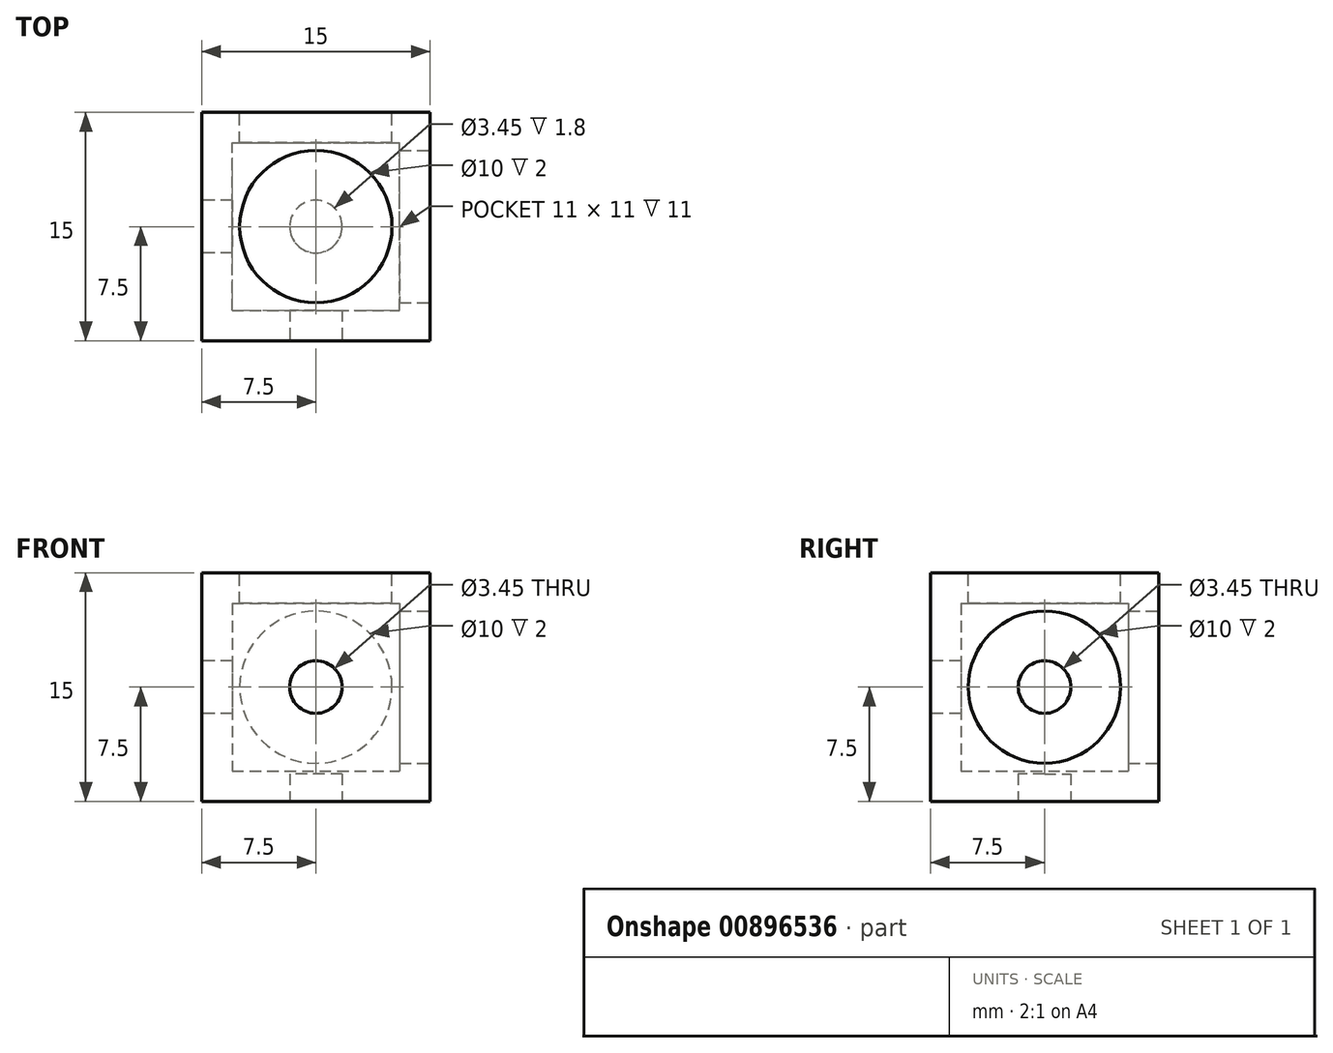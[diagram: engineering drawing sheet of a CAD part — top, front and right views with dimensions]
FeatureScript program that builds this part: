
annotation { "Feature Type Name" : "Feature", "Feature Type Description" : "" }
export const myFeature = defineFeature(function(context is Context, id is Id, definition is map)
    precondition{}
    {
        {
            var Q0;
            Q0=qCreatedBy(makeId("Top.planeOp"),FACE);
            var sketch = newSketch(context, id + "F0", { "sketchPlane" : qUnion([Q0])});
            skLineSegment(sketch, "E0.bottom", {"start": v(0, 0) * mm, "end": v(15, 0) * mm});
            skLineSegment(sketch, "E0.top", {"start": v(0, 15) * mm, "end": v(15, 15) * mm});
            skLineSegment(sketch, "E0.left", {"start": v(0, 0) * mm, "end": v(0, 15) * mm});
            skLineSegment(sketch, "E0.right", {"start": v(15, 0) * mm, "end": v(15, 15) * mm});
            skSolve(sketch);
        }
        {
            var Q0;
            Q0 = qSketchRegion(id + "F0", true);
            extrude(context, id + "F1", {"entities" : qUnion([Q0]), "depth" : 15 * mm, "offsetDistance" : 25 * mm});
        }
        {
            var Q0;
            Q0=qCreatedBy(makeId("Top.planeOp"),FACE);
            var sketch = newSketch(context, id + "F2", { "sketchPlane" : qUnion([Q0])});
            skLineSegment(sketch, "E1.bottom", {"start": v(2, 2) * mm, "end": v(13, 2) * mm});
            skLineSegment(sketch, "E1.top", {"start": v(2, 13) * mm, "end": v(13, 13) * mm});
            skLineSegment(sketch, "E1.left", {"start": v(2, 2) * mm, "end": v(2, 13) * mm});
            skLineSegment(sketch, "E1.right", {"start": v(13, 2) * mm, "end": v(13, 13) * mm});
            skLineSegment(sketch, "E2", {"start": v(2, 7.5) * mm, "end": v(0, 7.5) * mm, "construction": true});
            skLineSegment(sketch, "E3", {"start": v(7.5, 2) * mm, "end": v(7.5, 0) * mm, "construction": true});
            skSolve(sketch);
        }
        {
            var Q0;
            Q0 = qSketchRegion(id + "F2", true);
            extrude(context, id + "F3", {"entities" : qUnion([Q0]), "depth" : 11 * mm, "offsetDistance" : 25 * mm});
        }
        {
            var Q0;
            Q0=makeQuery(id+"F3.opExtrude","SWEPT_BODY",BODY,{"disambiguationData":[OSD([sQuery(id+"F2.wireOp",EDGE,"E1.bottom"),sQuery(id+"F2.wireOp",EDGE,"E1.top"),sQuery(id+"F2.wireOp",EDGE,"E1.left"),sQuery(id+"F2.wireOp",EDGE,"E1.right")])]});
            transform(context, id + "F4", {"entities" : qUnion([Q0]), "transformType" : TransformType.TRANSLATION_3D, "dx" : 0 * mm, "dy" : 0 * mm, "dz" : 2 * mm, "makeCopy" : false});
        }
        {
            var Q0;
            Q0=makeQuery(id+"F3.opExtrude","SWEPT_BODY",BODY,{"disambiguationData":[OSD([sQuery(id+"F2.wireOp",EDGE,"E1.bottom"),sQuery(id+"F2.wireOp",EDGE,"E1.top"),sQuery(id+"F2.wireOp",EDGE,"E1.left"),sQuery(id+"F2.wireOp",EDGE,"E1.right")])]});
            var Q1;
            Q1=makeQuery(id+"F1.opExtrude","SWEPT_BODY",BODY,{"disambiguationData":[OSD([sQuery(id+"F0.wireOp",EDGE,"E0.bottom"),sQuery(id+"F0.wireOp",EDGE,"E0.top"),sQuery(id+"F0.wireOp",EDGE,"E0.left"),sQuery(id+"F0.wireOp",EDGE,"E0.right")])]});
            booleanBodies(context, id + "F5", {"operationType" : BooleanOperationType.SUBTRACTION, "tools" : qUnion([Q0]), "targets" : qUnion([Q1])});
        }
        {
            var Q0;
            Q0=makeQuery(id+"F1.opExtrude","SWEPT_FACE",FACE,{"disambiguationData":[OSD([sQuery(id+"F0.wireOp",EDGE,"E0.bottom")])]});
            var sketch = newSketch(context, id + "F6", { "sketchPlane" : qUnion([Q0])});
            skLineSegment(sketch, "E4", {"start": v(0, 7.5) * mm, "end": v(7.5, 7.5) * mm, "construction": true});
            skLineSegment(sketch, "E5", {"start": v(7.5, 0) * mm, "end": v(7.5, 7.5) * mm, "construction": true});
            skCircle(sketch, "E6", {"center": v(7.5, 7.5) * mm, "radius": 1.73 * mm});
            skSolve(sketch);
        }
        {
            var Q0;
            Q0 = qSketchRegion(id + "F6", true);
            extrude(context, id + "F7", {"entities" : qUnion([Q0]), "operationType" : NewBodyOperationType.REMOVE, "endBound" : BoundingType.UP_TO_NEXT, "oppositeDirection" : true, "depth" : 15 * mm, "offsetDistance" : 25 * mm});
        }
        {
            var Q0;
            Q0=makeQuery(id+"F1.opExtrude","SWEPT_FACE",FACE,{"disambiguationData":[OSD([sQuery(id+"F0.wireOp",EDGE,"E0.left")])]});
            var sketch = newSketch(context, id + "F8", { "sketchPlane" : qUnion([Q0])});
            skLineSegment(sketch, "E7", {"start": v(-7.5, 0) * mm, "end": v(-7.5, 7.5) * mm, "construction": true});
            skLineSegment(sketch, "E8", {"start": v(-7.5, 7.5) * mm, "end": v(0, 7.5) * mm, "construction": true});
            skCircle(sketch, "E9", {"center": v(-7.5, 7.5) * mm, "radius": 1.73 * mm});
            skSolve(sketch);
        }
        {
            var Q0;
            Q0 = qSketchRegion(id + "F8", true);
            extrude(context, id + "F9", {"entities" : qUnion([Q0]), "operationType" : NewBodyOperationType.REMOVE, "endBound" : BoundingType.UP_TO_NEXT, "oppositeDirection" : true, "depth" : 15 * mm, "offsetDistance" : 25 * mm});
        }
        {
            var Q0;
            Q0=makeQuery(id+"F1.opExtrude","CAP_FACE",FACE,{"disambiguationData":[OSD([sQuery(id+"F0.wireOp",EDGE,"E0.bottom"),sQuery(id+"F0.wireOp",EDGE,"E0.top"),sQuery(id+"F0.wireOp",EDGE,"E0.left"),sQuery(id+"F0.wireOp",EDGE,"E0.right")])],"isStart":true});
            var sketch = newSketch(context, id + "F10", { "sketchPlane" : qUnion([Q0])});
            skLineSegment(sketch, "E10", {"start": v(0, -7.5) * mm, "end": v(7.5, -7.5) * mm, "construction": true});
            skLineSegment(sketch, "E11", {"start": v(7.5, -7.5) * mm, "end": v(7.5, -15) * mm, "construction": true});
            skCircle(sketch, "E12", {"center": v(7.5, -7.5) * mm, "radius": 1.73 * mm});
            skSolve(sketch);
        }
        {
            var Q0;
            Q0 = qSketchRegion(id + "F10", true);
            extrude(context, id + "F11", {"entities" : qUnion([Q0]), "operationType" : NewBodyOperationType.REMOVE, "endBound" : BoundingType.UP_TO_NEXT, "oppositeDirection" : true, "depth" : 15 * mm, "offsetDistance" : 25 * mm});
        }
        {
            var Q0;
            Q0=makeQuery(id+"F1.opExtrude","SWEPT_FACE",FACE,{"disambiguationData":[OSD([sQuery(id+"F0.wireOp",EDGE,"E0.top")])]});
            var sketch = newSketch(context, id + "F12", { "sketchPlane" : qUnion([Q0])});
            skCircle(sketch, "E13", {"center": v(-7.5, 7.5) * mm, "radius": 5 * mm});
            skLineSegment(sketch, "E14", {"start": v(-7.5, 7.5) * mm, "end": v(-15, 7.5) * mm, "construction": true});
            skLineSegment(sketch, "E15", {"start": v(-7.5, 7.5) * mm, "end": v(-7.5, 0) * mm, "construction": true});
            skSolve(sketch);
        }
        {
            var Q0;
            Q0 = qSketchRegion(id + "F12", true);
            extrude(context, id + "F13", {"entities" : qUnion([Q0]), "operationType" : NewBodyOperationType.REMOVE, "oppositeDirection" : true, "depth" : (15 / 2) * mm, "offsetDistance" : 25 * mm});
        }
        {
            var Q0;
            Q0=makeQuery(id+"F1.opExtrude","SWEPT_FACE",FACE,{"disambiguationData":[OSD([sQuery(id+"F0.wireOp",EDGE,"E0.right")])]});
            var sketch = newSketch(context, id + "F14", { "sketchPlane" : qUnion([Q0])});
            skCircle(sketch, "E16", {"center": v(7.5, 7.5) * mm, "radius": 5 * mm});
            skLineSegment(sketch, "E17", {"start": v(7.5, 7.5) * mm, "end": v(0, 7.5) * mm, "construction": true});
            skLineSegment(sketch, "E18", {"start": v(7.5, 7.5) * mm, "end": v(7.5, 0) * mm, "construction": true});
            skSolve(sketch);
        }
        {
            var Q0;
            Q0 = qSketchRegion(id + "F14", true);
            extrude(context, id + "F15", {"entities" : qUnion([Q0]), "operationType" : NewBodyOperationType.REMOVE, "oppositeDirection" : true, "depth" : (15 / 2) * mm, "offsetDistance" : 25 * mm});
        }
        {
            var Q0;
            Q0=makeQuery(id+"F1.opExtrude","CAP_FACE",FACE,{"disambiguationData":[OSD([sQuery(id+"F0.wireOp",EDGE,"E0.bottom"),sQuery(id+"F0.wireOp",EDGE,"E0.top"),sQuery(id+"F0.wireOp",EDGE,"E0.left"),sQuery(id+"F0.wireOp",EDGE,"E0.right")])],"isStart":false});
            var sketch = newSketch(context, id + "F16", { "sketchPlane" : qUnion([Q0])});
            skCircle(sketch, "E19", {"center": v(7.5, 7.5) * mm, "radius": 5 * mm});
            skLineSegment(sketch, "E20", {"start": v(7.5, 7.5) * mm, "end": v(0, 7.5) * mm, "construction": true});
            skLineSegment(sketch, "E21", {"start": v(7.5, 7.5) * mm, "end": v(7.5, 0) * mm, "construction": true});
            skSolve(sketch);
        }
        {
            var Q0;
            Q0 = qSketchRegion(id + "F16", true);
            extrude(context, id + "F17", {"entities" : qUnion([Q0]), "operationType" : NewBodyOperationType.REMOVE, "oppositeDirection" : true, "depth" : (15 / 2) * mm, "offsetDistance" : 25 * mm});
        }
        {
            var Q0;
            Q0=makeQuery(id+"F1.opExtrude","SWEPT_FACE",FACE,{"disambiguationData":[OSD([sQuery(id+"F0.wireOp",EDGE,"E0.top")])]});
            var sketch = newSketch(context, id + "F18", { "sketchPlane" : qUnion([Q0])});
            skCircle(sketch, "E22", {"center": v(-7.5, 7.5) * mm, "radius": 3.5 * mm});
            skSolve(sketch);
        }
        {
            var Q0;
            Q0 = qSketchRegion(id + "F18", true);
            extrude(context, id + "F19", {"entities" : qUnion([Q0]), "operationType" : NewBodyOperationType.REMOVE, "oppositeDirection" : true, "depth" : 13 * mm, "offsetDistance" : 25 * mm});
        }
        {
            var Q0;
            Q0=makeQuery(id+"F1.opExtrude","SWEPT_FACE",FACE,{"disambiguationData":[OSD([sQuery(id+"F0.wireOp",EDGE,"E0.right")])]});
            var sketch = newSketch(context, id + "F20", { "sketchPlane" : qUnion([Q0])});
            skCircle(sketch, "E23", {"center": v(7.5, 7.5) * mm, "radius": 3.5 * mm});
            skSolve(sketch);
        }
        {
            var Q0;
            Q0 = qSketchRegion(id + "F20", true);
            extrude(context, id + "F21", {"entities" : qUnion([Q0]), "operationType" : NewBodyOperationType.REMOVE, "oppositeDirection" : true, "depth" : 13 * mm, "offsetDistance" : 25 * mm});
        }
        {
            var Q0;
            Q0=makeQuery(id+"F1.opExtrude","CAP_FACE",FACE,{"disambiguationData":[OSD([sQuery(id+"F0.wireOp",EDGE,"E0.bottom"),sQuery(id+"F0.wireOp",EDGE,"E0.top"),sQuery(id+"F0.wireOp",EDGE,"E0.left"),sQuery(id+"F0.wireOp",EDGE,"E0.right")])],"isStart":false});
            var sketch = newSketch(context, id + "F22", { "sketchPlane" : qUnion([Q0])});
            skCircle(sketch, "E24", {"center": v(7.5, 7.5) * mm, "radius": 3.5 * mm});
            skSolve(sketch);
        }
        {
            var Q0;
            Q0 = qSketchRegion(id + "F22", true);
            extrude(context, id + "F23", {"entities" : qUnion([Q0]), "operationType" : NewBodyOperationType.REMOVE, "oppositeDirection" : true, "depth" : 13 * mm, "offsetDistance" : 25 * mm});
        }
        {
            var Q0;
            Q0=makeQuery(id+"F5.opBoolean","COPY",FACE,{"derivedFrom":makeQuery(id+"F3.opExtrude","CAP_FACE",FACE,{"disambiguationData":[OSD([sQuery(id+"F2.wireOp",EDGE,"E1.bottom"),sQuery(id+"F2.wireOp",EDGE,"E1.top"),sQuery(id+"F2.wireOp",EDGE,"E1.left"),sQuery(id+"F2.wireOp",EDGE,"E1.right")])],"isStart":true})});
            var sketch = newSketch(context, id + "F24", { "sketchPlane" : qUnion([Q0])});
            skCircle(sketch, "E25", {"center": v(7.5, 7.5) * mm, "radius": 1.73 * mm});
            skSolve(sketch);
        }
        {
            var Q0;
            Q0 = qSketchRegion(id + "F24", true);
            extrude(context, id + "F25", {"entities" : qUnion([Q0]), "operationType" : NewBodyOperationType.ADD, "oppositeDirection" : true, "depth" : 0.2 * mm, "offsetDistance" : 25 * mm});
        }
    });
